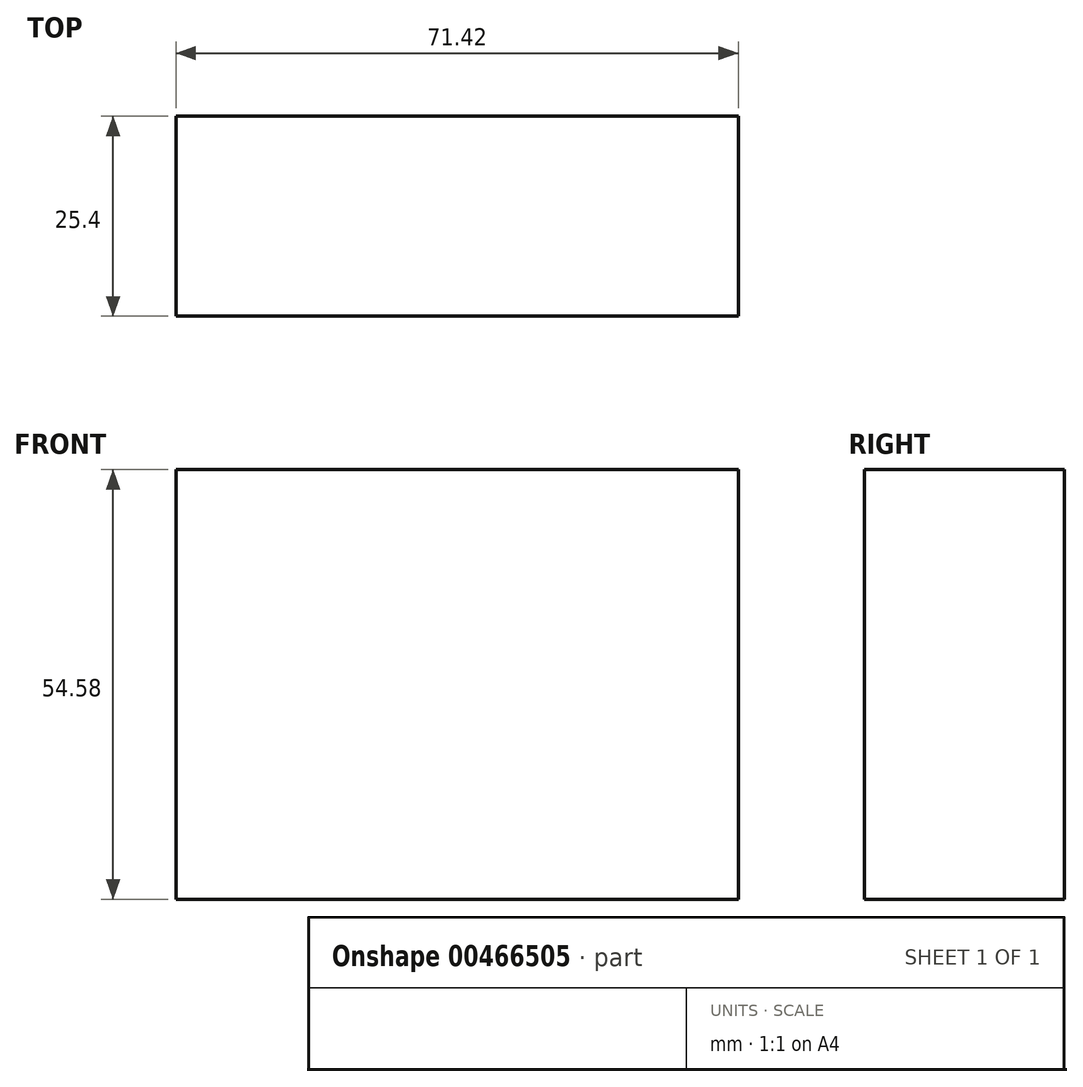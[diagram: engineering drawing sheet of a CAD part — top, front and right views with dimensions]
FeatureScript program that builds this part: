
annotation { "Feature Type Name" : "Feature", "Feature Type Description" : "" }
export const myFeature = defineFeature(function(context is Context, id is Id, definition is map)
    precondition{}
    {
        {
            var Q0;
            Q0=qCreatedBy(makeId("Front.planeOp"),FACE);
            var sketch = newSketch(context, id + "F0", { "sketchPlane" : qUnion([Q0])});
            skLineSegment(sketch, "E0.bottom", {"start": v(-35.38, 34.08) * mm, "end": v(36.04, 34.08) * mm});
            skLineSegment(sketch, "E0.top", {"start": v(-35.38, -20.5) * mm, "end": v(36.04, -20.5) * mm});
            skLineSegment(sketch, "E0.left", {"start": v(-35.38, 34.08) * mm, "end": v(-35.38, -20.5) * mm});
            skLineSegment(sketch, "E0.right", {"start": v(36.04, 34.08) * mm, "end": v(36.04, -20.5) * mm});
            skSolve(sketch);
        }
        {
            var Q0;
            Q0=makeQuery(id+"F0.imprint","IMPRINT",FACE,{"disambiguationData":[TD([[makeQuery(id+"F0.imprint","IMPRINT",EDGE,{"derivedFrom":sQuery(id+"F0.wireOp",EDGE,"E0.bottom")}),-1.0]])]});
            extrude(context, id + "F1", {"entities" : qUnion([Q0]), "depth" : 25.4 * mm});
        }
        {
            var Q0;
            Q0=qCreatedBy(makeId("Front.planeOp"),FACE);
            var sketch = newSketch(context, id + "F2", { "sketchPlane" : qUnion([Q0])});
            skCircle(sketch, "E1", {"center": v(0, 0) * mm, "radius": 19.67 * mm});
            skCircle(sketch, "E2", {"center": v(0, 0) * mm, "radius": 15.5 * mm});
            skSolve(sketch);
        }
        {
            var Q0;
            Q0=sQuery(id+"F2.wireOp",EDGE,"E2");
            var Q1;
            Q1=sQuery(id+"F2.wireOp",EDGE,"E1");
            extrude(context, id + "F3", {"bodyType" : ToolBodyType.SURFACE, "surfaceEntities" : qUnion([Q0, Q1]), "depth" : 36.58 * mm});
        }
    });
